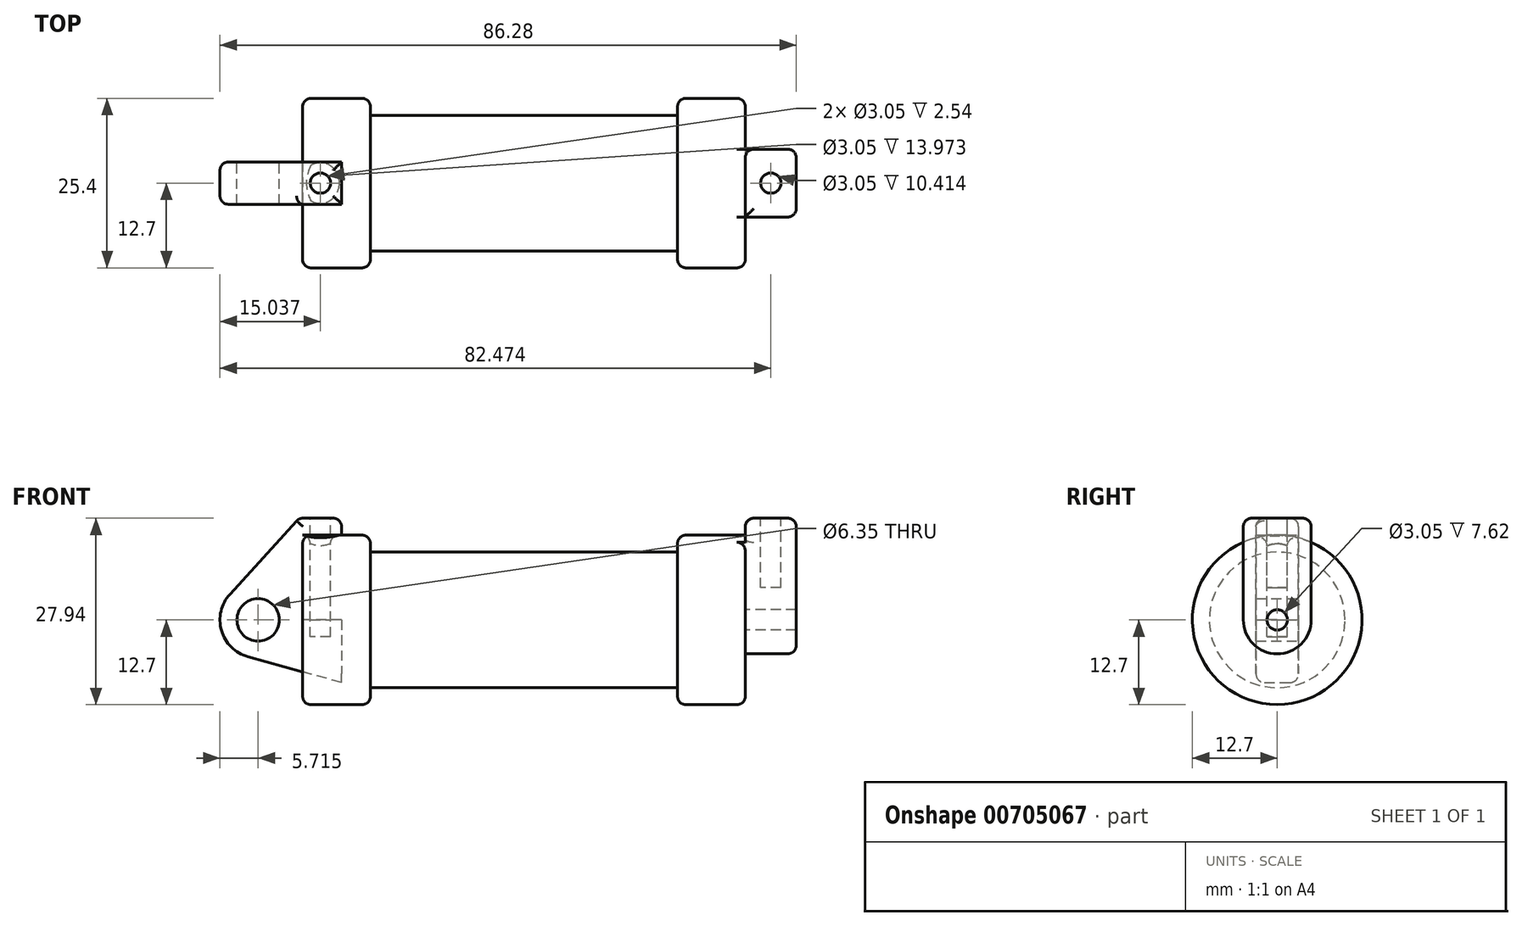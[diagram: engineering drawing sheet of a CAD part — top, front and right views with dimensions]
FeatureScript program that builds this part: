
annotation { "Feature Type Name" : "Feature", "Feature Type Description" : "" }
export const myFeature = defineFeature(function(context is Context, id is Id, definition is map)
    precondition{}
    {
        {
            var Q0;
            Q0=qCreatedBy(makeId("Front.planeOp"),FACE);
            var sketch = newSketch(context, id + "F0", { "sketchPlane" : qUnion([Q0])});
            skLineSegment(sketch, "E0", {"start": v(0, 0) * mm, "end": v(0, 12.7) * mm});
            skLineSegment(sketch, "E1", {"start": v(0, 12.7) * mm, "end": v(10.16, 12.7) * mm});
            skLineSegment(sketch, "E2", {"start": v(10.16, 12.7) * mm, "end": v(10.16, 10.16) * mm});
            skLineSegment(sketch, "E3", {"start": v(10.16, 10.16) * mm, "end": v(56.13, 10.16) * mm});
            skLineSegment(sketch, "E4", {"start": v(56.13, 10.16) * mm, "end": v(56.13, 12.7) * mm});
            skLineSegment(sketch, "E5", {"start": v(56.13, 12.7) * mm, "end": v(66.3, 12.7) * mm});
            skLineSegment(sketch, "E6", {"start": v(66.3, 12.7) * mm, "end": v(66.3, 0) * mm});
            skLineSegment(sketch, "E7", {"start": v(66.3, 0) * mm, "end": v(0, 0) * mm});
            skLineSegment(sketch, "E8", {"start": v(5.84, 15.24) * mm, "end": v(-0.5, 15.24) * mm});
            skLineSegment(sketch, "E9", {"start": v(-0.5, 15.24) * mm, "end": v(-10.88, 3.85) * mm});
            skLineSegment(sketch, "E10", {"start": v(0, 0) * mm, "end": v(-6.65, 0) * mm});
            skCircle(sketch, "E11", {"center": v(-6.65, 0) * mm, "radius": 5.72 * mm});
            skCircle(sketch, "E12", {"center": v(-6.65, 0) * mm, "radius": 3.18 * mm});
            skLineSegment(sketch, "E13", {"start": v(5.84, 15.24) * mm, "end": v(5.84, -9.4) * mm});
            skLineSegment(sketch, "E14", {"start": v(5.84, -9.4) * mm, "end": v(-8.18, -5.5) * mm});
            skSolve(sketch);
        }
        {
            var Q0;
            {var subQ0=sQuery(id+"F0.wireOp",EDGE,"E2");Q0=makeQuery(id+"F0.imprint","IMPRINT",FACE,{"disambiguationData":[TD([[makeQuery(id+"F0.imprint","IMPRINT",EDGE,{"derivedFrom":subQ0}),-1.0]])]});}
            var Q1;
            {var subQ0=sQuery(id+"F0.wireOp",EDGE,"E0");Q1=makeQuery(id+"F0.imprint","IMPRINT",FACE,{"disambiguationData":[TD([[makeQuery(id+"F0.imprint","IMPRINT",EDGE,{"derivedFrom":subQ0}),-1.0]])]});}
            var Q2;
            Q2=sQuery(id+"F0.wireOp",EDGE,"E7");
            revolve(context, id + "F1", {"entities" : qUnion([Q0, Q1]), "axis" : qUnion([Q2]), "revolveType" : RevolveType.FULL});
        }
        {
            var Q0;
            {var subQ1=sQuery(id+"F0.wireOp",EDGE,"E0");Q0=makeQuery(id+"F0.imprint","IMPRINT",FACE,{"disambiguationData":[TD([[makeQuery(id+"F0.imprint","IMPRINT",EDGE,{"derivedFrom":subQ1}),1.0]])]});}
            var Q1;
            {var subQ5=sQuery(id+"F0.wireOp",EDGE,"E12");Q1=makeQuery(id+"F0.imprint","IMPRINT",FACE,{"disambiguationData":[TD([[makeQuery(id+"F0.imprint","IMPRINT",EDGE,{"derivedFrom":subQ5}),-1.0]])]});}
            var Q2;
            {var subQ0=sQuery(id+"F0.wireOp",EDGE,"E14");Q2=makeQuery(id+"F0.imprint","IMPRINT",FACE,{"disambiguationData":[TD([[makeQuery(id+"F0.imprint","IMPRINT",EDGE,{"derivedFrom":subQ0}),-1.0]])]});}
            extrude(context, id + "F2", {"entities" : qUnion([Q0, Q1, Q2]), "depth" : 6.35 * mm, "offsetDistance" : 25.4 * mm, "symmetric" : true});
        }
        {
            var Q0;
            Q0=makeQuery(id+"F1.opRevolve","SWEPT_FACE",FACE,{"disambiguationData":[OSD([sQuery(id+"F0.wireOp",EDGE,"E6")])]});
            var sketch = newSketch(context, id + "F3", { "sketchPlane" : qUnion([Q0])});
            skCircle(sketch, "E15", {"center": v(0, 0) * mm, "radius": 1.52 * mm});
            skCircle(sketch, "E16", {"center": v(0, 0) * mm, "radius": 5.08 * mm});
            skLineSegment(sketch, "E17", {"start": v(5.08, 0) * mm, "end": v(5.08, 15.24) * mm});
            skLineSegment(sketch, "E18", {"start": v(5.08, 15.24) * mm, "end": v(-5.08, 15.24) * mm});
            skLineSegment(sketch, "E19", {"start": v(-5.08, 0) * mm, "end": v(-5.08, 15.24) * mm});
            skSolve(sketch);
        }
        {
            var Q0;
            Q0 = qSketchRegion(id + "F3", true);
            extrude(context, id + "F4", {"entities" : qUnion([Q0]), "operationType" : NewBodyOperationType.ADD, "depth" : 7.62 * mm, "offsetDistance" : 25.4 * mm});
        }
        {
            var Q0;
            Q0=makeQuery(id+"F2.opExtrude","SWEPT_FACE",FACE,{"disambiguationData":[OSD([sQuery(id+"F0.wireOp",EDGE,"E8")])]});
            var sketch = newSketch(context, id + "F5", { "sketchPlane" : qUnion([Q0])});
            skCircle(sketch, "E20", {"center": v(2.67, 0) * mm, "radius": 1.52 * mm});
            skPoint(sketch, "E20.centerSnap0", {"position": v(5.84, 0) * mm});
            skPoint(sketch, "E20.centerSnap1", {"position": v(2.67, 3.18) * mm});
            skSolve(sketch);
        }
        {
            var Q0;
            Q0=makeQuery(id+"F4.opExtrude","SWEPT_FACE",FACE,{"disambiguationData":[OSD([sQuery(id+"F3.wireOp",EDGE,"E18")])]});
            var sketch = newSketch(context, id + "F6", { "sketchPlane" : qUnion([Q0])});
            skCircle(sketch, "E21", {"center": v(70.1, 0) * mm, "radius": 1.52 * mm});
            skPoint(sketch, "E21.centerSnap0", {"position": v(73.91, 0) * mm});
            skPoint(sketch, "E21.centerSnap1", {"position": v(70.1, 5.08) * mm});
            skSolve(sketch);
        }
        {
            var Q0;
            Q0=makeQuery(id+"F5.imprint","IMPRINT",FACE,{"disambiguationData":[TD([[makeQuery(id+"F5.imprint","IMPRINT",EDGE,{"derivedFrom":sQuery(id+"F5.wireOp",EDGE,"E20")}),1.0]])]});
            var Q1;
            Q1=sQuery(id+"F5.wireOp",EDGE,"E20");
            extrude(context, id + "F7", {"entities" : qUnion([Q0]), "operationType" : NewBodyOperationType.REMOVE, "surfaceEntities" : qUnion([Q1]), "oppositeDirection" : true, "depth" : 17.78 * mm, "offsetDistance" : 25.4 * mm});
        }
        {
            var Q0;
            Q0=makeQuery(id+"F6.imprint","IMPRINT",FACE,{"disambiguationData":[TD([[makeQuery(id+"F6.imprint","IMPRINT",EDGE,{"derivedFrom":sQuery(id+"F6.wireOp",EDGE,"E21")}),1.0]])]});
            extrude(context, id + "F8", {"entities" : qUnion([Q0]), "operationType" : NewBodyOperationType.REMOVE, "oppositeDirection" : true, "depth" : 10.4 * mm, "offsetDistance" : 25.4 * mm});
        }
        {
            var Q0;
            {var subQ0=sQuery(id+"F0.wireOp",EDGE,"E5");var subQ1=sQuery(id+"F0.wireOp",EDGE,"E6");Q0=makeQuery(id+"F4.boolean.opBoolean","SPLIT",EDGE,{"disambiguationData":[topologyDisambiguationEdgeConnected([makeQuery(id+"F1.opRevolve","SWEPT_FACE",FACE,{"disambiguationData":[OSD([subQ1])]})])],"derivedFrom":makeQuery(id+"F1.opRevolve","SWEPT_EDGE",EDGE,{"disambiguationData":[OSD([subQ0,subQ1])]})});}
            fillet(context, id + "F9", {"entities" : qUnion([Q0]), "radius" : 1.27 * mm, "tangentPropagation" : true, "allowEdgeOverflow" : false});
        }
        {
            var Q0;
            Q0=makeQuery(id+"F2.opExtrude","CAP_EDGE",EDGE,{"disambiguationData":[OSD([sQuery(id+"F0.wireOp",EDGE,"E9")])],"isStart":false});
            fillet(context, id + "F10", {"entities" : qUnion([Q0]), "radius" : 1.27 * mm, "tangentPropagation" : true, "allowEdgeOverflow" : false});
        }
        {
            var Q0;
            Q0=makeQuery(id+"F1.opRevolve","SWEPT_FACE",FACE,{"disambiguationData":[OSD([sQuery(id+"F0.wireOp",EDGE,"E1")])]});
            var Q1;
            Q1=makeQuery(id+"F2.opExtrude","CAP_EDGE",EDGE,{"disambiguationData":[OSD([sQuery(id+"F0.wireOp",EDGE,"E9")])],"isStart":true});
            var Q2;
            Q2=makeQuery(id+"F2.opExtrude","CAP_EDGE",EDGE,{"disambiguationData":[OSD([sQuery(id+"F0.wireOp",EDGE,"E8")])],"isStart":true});
            var Q3;
            Q3=makeQuery(id+"F2.opExtrude","SWEPT_EDGE",EDGE,{"disambiguationData":[OSD([sQuery(id+"F0.wireOp",EDGE,"E8"),sQuery(id+"F0.wireOp",EDGE,"E13")])]});
            var Q4;
            Q4=makeQuery(id+"F2.opExtrude","CAP_EDGE",EDGE,{"disambiguationData":[OSD([sQuery(id+"F0.wireOp",EDGE,"E8")])],"isStart":false});
            var Q5;
            Q5=makeQuery(id+"F1.opRevolve","SWEPT_EDGE",EDGE,{"disambiguationData":[OSD([sQuery(id+"F0.wireOp",EDGE,"E4"),sQuery(id+"F0.wireOp",EDGE,"E5")])]});
            var Q6;
            Q6=makeQuery(id+"F4.opExtrude","CAP_EDGE",EDGE,{"disambiguationData":[OSD([sQuery(id+"F3.wireOp",EDGE,"E17")])],"isStart":false});
            var Q7;
            Q7=makeQuery(id+"F4.opExtrude","CAP_EDGE",EDGE,{"disambiguationData":[OSD([sQuery(id+"F3.wireOp",EDGE,"E18")])],"isStart":true});
            var Q8;
            Q8=makeQuery(id+"F4.opExtrude","CAP_EDGE",EDGE,{"disambiguationData":[OSD([sQuery(id+"F3.wireOp",EDGE,"E18")])],"isStart":false});
            var Q9;
            Q9=makeQuery(id+"F4.opExtrude","SWEPT_EDGE",EDGE,{"disambiguationData":[OSD([sQuery(id+"F3.wireOp",EDGE,"E17"),sQuery(id+"F3.wireOp",EDGE,"E18")])]});
            var Q10;
            Q10=makeQuery(id+"F4.opExtrude","SWEPT_EDGE",EDGE,{"disambiguationData":[OSD([sQuery(id+"F3.wireOp",EDGE,"E18"),sQuery(id+"F3.wireOp",EDGE,"E19")])]});
            fillet(context, id + "F11", {"entities" : qUnion([Q0, Q1, Q2, Q3, Q4, Q5, Q6, Q7, Q8, Q9, Q10]), "radius" : 1.27 * mm, "tangentPropagation" : true, "allowEdgeOverflow" : false});
        }
        {
            var Q0;
            {var subQ0=sQuery(id+"F3.wireOp",EDGE,"E17");Q0=makeQuery(id+"F4.boolean.opBoolean","SPLIT",EDGE,{"disambiguationData":[topologyDisambiguationEdgeConnected([makeQuery(id+"F1.opRevolve","SWEPT_FACE",FACE,{"disambiguationData":[OSD([sQuery(id+"F0.wireOp",EDGE,"E6")])]})])],"derivedFrom":makeQuery(id+"F4.opExtrude","CAP_EDGE",EDGE,{"disambiguationData":[OSD([subQ0])],"isStart":true})});}
            fillet(context, id + "F12", {"entities" : qUnion([Q0]), "radius" : 1.27 * mm, "tangentPropagation" : true, "allowEdgeOverflow" : false});
        }
    });
